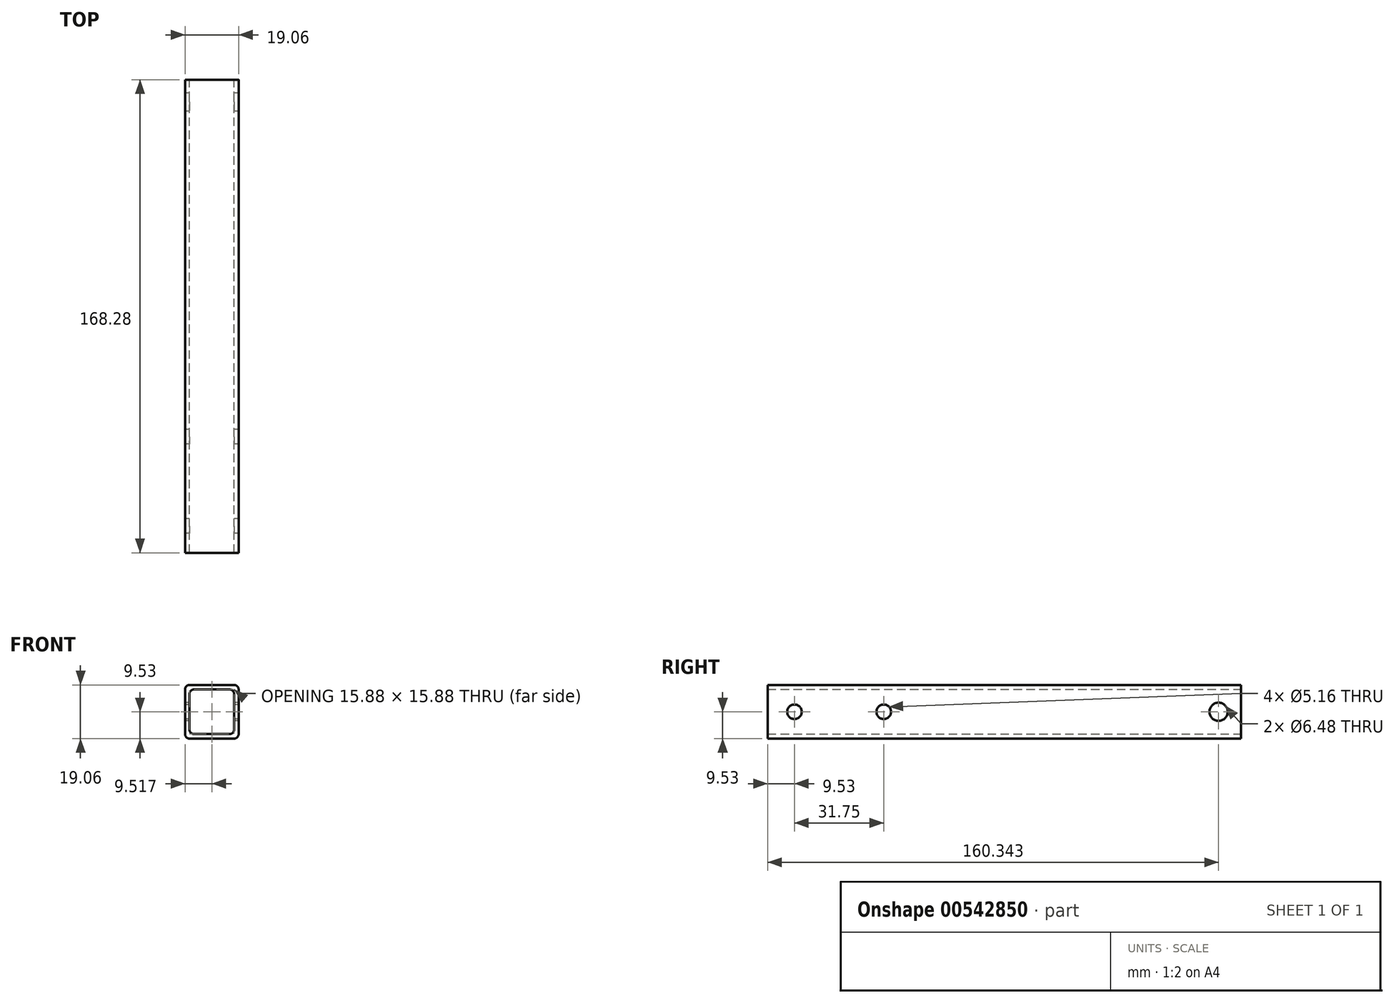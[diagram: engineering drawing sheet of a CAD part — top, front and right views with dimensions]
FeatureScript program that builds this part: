
annotation { "Feature Type Name" : "Feature", "Feature Type Description" : "" }
export const myFeature = defineFeature(function(context is Context, id is Id, definition is map)
    precondition{}
    {
        {
            var Q0;
            Q0=qCreatedBy(makeId("Front.planeOp"),FACE);
            var sketch = newSketch(context, id + "F0", { "sketchPlane" : qUnion([Q0])});
            skLineSegment(sketch, "E0.bottom", {"start": v(-9.53, 9.53) * mm, "end": v(9.53, 9.53) * mm});
            skLineSegment(sketch, "E0.top", {"start": v(-9.53, -9.53) * mm, "end": v(9.53, -9.53) * mm});
            skLineSegment(sketch, "E0.left", {"start": v(-9.53, 9.53) * mm, "end": v(-9.53, -9.53) * mm});
            skLineSegment(sketch, "E0.right", {"start": v(9.53, 9.53) * mm, "end": v(9.53, -9.53) * mm});
            skPoint(sketch, "E1", {"position": v(-9.53, 0) * mm});
            skPoint(sketch, "E2", {"position": v(9.53, 0) * mm});
            skPoint(sketch, "E3", {"position": v(0, -9.53) * mm});
            skPoint(sketch, "E4", {"position": v(0, 9.53) * mm});
            skLineSegment(sketch, "E5.bottom", {"start": v(-7.95, 7.94) * mm, "end": v(7.92, 7.94) * mm});
            skLineSegment(sketch, "E5.top", {"start": v(-7.95, -7.94) * mm, "end": v(7.92, -7.94) * mm});
            skLineSegment(sketch, "E5.left", {"start": v(-7.95, 7.94) * mm, "end": v(-7.95, -7.94) * mm});
            skLineSegment(sketch, "E5.right", {"start": v(7.92, 7.94) * mm, "end": v(7.92, -7.94) * mm});
            skSolve(sketch);
        }
        {
            var Q0;
            Q0=qSketchRegion(id+"F0",true);
            extrude(context, id + "F1", {"entities" : qUnion([Q0]), "depth" : 215.9 * mm, "offsetDistance" : 25.4 * mm, "symmetric" : true});
        }
        {
            var Q0;
            Q0=makeQuery(id+"F1.opExtrude","SWEPT_EDGE",EDGE,{"disambiguationData":[OSD([sQuery(id+"F0.wireOp",EDGE,"E0.bottom"),sQuery(id+"F0.wireOp",EDGE,"E0.left")])]});
            var Q1;
            Q1=makeQuery(id+"F1.opExtrude","SWEPT_EDGE",EDGE,{"disambiguationData":[OSD([sQuery(id+"F0.wireOp",EDGE,"E0.top"),sQuery(id+"F0.wireOp",EDGE,"E0.left")])]});
            var Q2;
            Q2=makeQuery(id+"F1.opExtrude","SWEPT_EDGE",EDGE,{"disambiguationData":[OSD([sQuery(id+"F0.wireOp",EDGE,"E0.top"),sQuery(id+"F0.wireOp",EDGE,"E0.right")])]});
            var Q3;
            Q3=makeQuery(id+"F1.opExtrude","SWEPT_EDGE",EDGE,{"disambiguationData":[OSD([sQuery(id+"F0.wireOp",EDGE,"E0.bottom"),sQuery(id+"F0.wireOp",EDGE,"E0.right")])]});
            fillet(context, id + "F2", {"entities" : qUnion([Q0, Q1, Q2, Q3]), "radius" : 1.59 * mm, "tangentPropagation" : true, "allowEdgeOverflow" : false});
        }
        {
            var Q0;
            Q0=makeQuery(id+"F1.opExtrude","SWEPT_EDGE",EDGE,{"disambiguationData":[OSD([sQuery(id+"F0.wireOp",EDGE,"E5.bottom"),sQuery(id+"F0.wireOp",EDGE,"E5.left")])]});
            var Q1;
            Q1=makeQuery(id+"F1.opExtrude","SWEPT_EDGE",EDGE,{"disambiguationData":[OSD([sQuery(id+"F0.wireOp",EDGE,"E5.top"),sQuery(id+"F0.wireOp",EDGE,"E5.left")])]});
            var Q2;
            Q2=makeQuery(id+"F1.opExtrude","SWEPT_EDGE",EDGE,{"disambiguationData":[OSD([sQuery(id+"F0.wireOp",EDGE,"E5.bottom"),sQuery(id+"F0.wireOp",EDGE,"E5.right")])]});
            var Q3;
            Q3=makeQuery(id+"F1.opExtrude","SWEPT_EDGE",EDGE,{"disambiguationData":[OSD([sQuery(id+"F0.wireOp",EDGE,"E5.top"),sQuery(id+"F0.wireOp",EDGE,"E5.right")])]});
            fillet(context, id + "F3", {"entities" : qUnion([Q0, Q1, Q2, Q3]), "radius" : 1.59 * mm, "tangentPropagation" : true, "allowEdgeOverflow" : false});
        }
        {
            var Q0;
            Q0=makeQuery(id+"F1.opExtrude","SWEPT_FACE",FACE,{"disambiguationData":[OSD([sQuery(id+"F0.wireOp",EDGE,"E0.left")])]});
            var sketch = newSketch(context, id + "F4", { "sketchPlane" : qUnion([Q0])});
            skCircle(sketch, "E6", {"center": v(-100.01, 0) * mm, "radius": 3.24 * mm});
            skCircle(sketch, "E7", {"center": v(19.05, 0) * mm, "radius": 2.58 * mm});
            skPoint(sketch, "E7.centerSnap0", {"position": v(-107.95, 0) * mm});
            skCircle(sketch, "E8", {"center": v(50.8, 0) * mm, "radius": 2.58 * mm});
            skSolve(sketch);
        }
        {
            var Q0;
            Q0=makeQuery(id+"F4.imprint","IMPRINT",FACE,{"disambiguationData":[TD([[makeQuery(id+"F4.imprint","IMPRINT",EDGE,{"derivedFrom":sQuery(id+"F4.wireOp",EDGE,"E6")}),1.0]])]});
            var Q1;
            Q1=makeQuery(id+"F4.imprint","IMPRINT",FACE,{"disambiguationData":[TD([[makeQuery(id+"F4.imprint","IMPRINT",EDGE,{"derivedFrom":sQuery(id+"F4.wireOp",EDGE,"E7")}),1.0]])]});
            var Q2;
            Q2=makeQuery(id+"F4.imprint","IMPRINT",FACE,{"disambiguationData":[TD([[makeQuery(id+"F4.imprint","IMPRINT",EDGE,{"derivedFrom":sQuery(id+"F4.wireOp",EDGE,"E8")}),1.0]])]});
            var Q3;
            Q3=sQuery(id+"F4.wireOp",EDGE,"E6");
            var Q4;
            Q4=sQuery(id+"F4.wireOp",EDGE,"E7");
            var Q5;
            Q5=sQuery(id+"F4.wireOp",EDGE,"E8");
            extrude(context, id + "F5", {"entities" : qUnion([Q0, Q1, Q2]), "operationType" : NewBodyOperationType.REMOVE, "surfaceEntities" : qUnion([Q3, Q4, Q5]), "oppositeDirection" : true, "depth" : 19.05 * mm, "offsetDistance" : 25.4 * mm});
        }
        {
            var Q0;
            Q0=makeQuery(id+"F1.opExtrude","CAP_FACE",FACE,{"disambiguationData":[OSD([sQuery(id+"F0.wireOp",EDGE,"E0.bottom"),sQuery(id+"F0.wireOp",EDGE,"E0.top"),sQuery(id+"F0.wireOp",EDGE,"E0.left"),sQuery(id+"F0.wireOp",EDGE,"E0.right"),sQuery(id+"F0.wireOp",EDGE,"E5.bottom"),sQuery(id+"F0.wireOp",EDGE,"E5.top"),sQuery(id+"F0.wireOp",EDGE,"E5.left"),sQuery(id+"F0.wireOp",EDGE,"E5.right")])],"isStart":false});
            extrude(context, id + "F6", {"entities" : qUnion([Q0]), "operationType" : NewBodyOperationType.REMOVE, "oppositeDirection" : true, "depth" : 47.62 * mm, "offsetDistance" : 25.4 * mm});
        }
        {
            var Q0;
            Q0=makeQuery(id+"F1.opExtrude","CAP_FACE",FACE,{"disambiguationData":[OSD([sQuery(id+"F0.wireOp",EDGE,"E0.bottom"),sQuery(id+"F0.wireOp",EDGE,"E0.top"),sQuery(id+"F0.wireOp",EDGE,"E0.left"),sQuery(id+"F0.wireOp",EDGE,"E0.right"),sQuery(id+"F0.wireOp",EDGE,"E5.bottom"),sQuery(id+"F0.wireOp",EDGE,"E5.top"),sQuery(id+"F0.wireOp",EDGE,"E5.left"),sQuery(id+"F0.wireOp",EDGE,"E5.right")])],"isStart":true});
            extrude(context, id + "F7", {"entities" : qUnion([Q0]), "operationType" : NewBodyOperationType.REMOVE, "depth" : -1 / 203.2 * mm, "offsetDistance" : 25.4 * mm});
        }
    });
